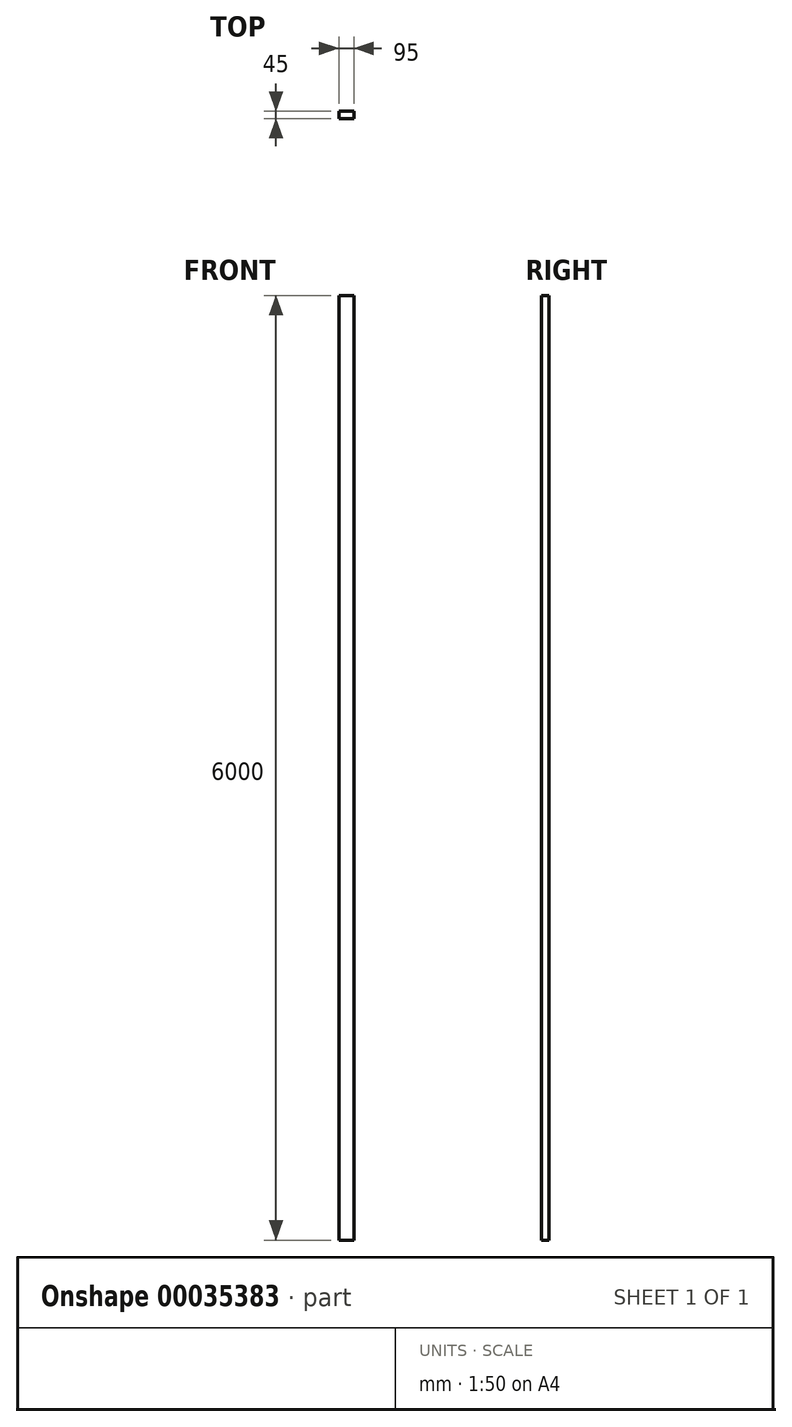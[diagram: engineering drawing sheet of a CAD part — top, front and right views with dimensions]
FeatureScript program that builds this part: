
annotation { "Feature Type Name" : "Feature", "Feature Type Description" : "" }
export const myFeature = defineFeature(function(context is Context, id is Id, definition is map)
    precondition{}
    {
        {
            var Q0;
            Q0=qCreatedBy(makeId("Top.planeOp"),FACE);
            var sketch = newSketch(context, id + "F0", { "sketchPlane" : qUnion([Q0])});
            skLineSegment(sketch, "E0.rect.bottom", {"start": v(47.5, -22.5) * mm, "end": v(-47.5, -22.5) * mm});
            skLineSegment(sketch, "E0.rect.top", {"start": v(47.5, 22.5) * mm, "end": v(-47.5, 22.5) * mm});
            skLineSegment(sketch, "E0.rect.left", {"start": v(47.5, -22.5) * mm, "end": v(47.5, 22.5) * mm});
            skLineSegment(sketch, "E0.rect.right", {"start": v(-47.5, -22.5) * mm, "end": v(-47.5, 22.5) * mm});
            skPoint(sketch, "E0.rect.middle", {"position": v(0, 0) * mm});
            skSolve(sketch);
        }
        {
            var Q0;
            Q0=makeQuery(id+"F0.imprint","IMPRINT",FACE,{"disambiguationData":[TD([[makeQuery(id+"F0.imprint","IMPRINT",EDGE,{"derivedFrom":sQuery(id+"F0.wireOp",EDGE,"E0.rect.bottom")}),-1.0]])]});
            extrude(context, id + "F1", {"entities" : qUnion([Q0]), "depth" : 6000 * mm});
        }
    });
